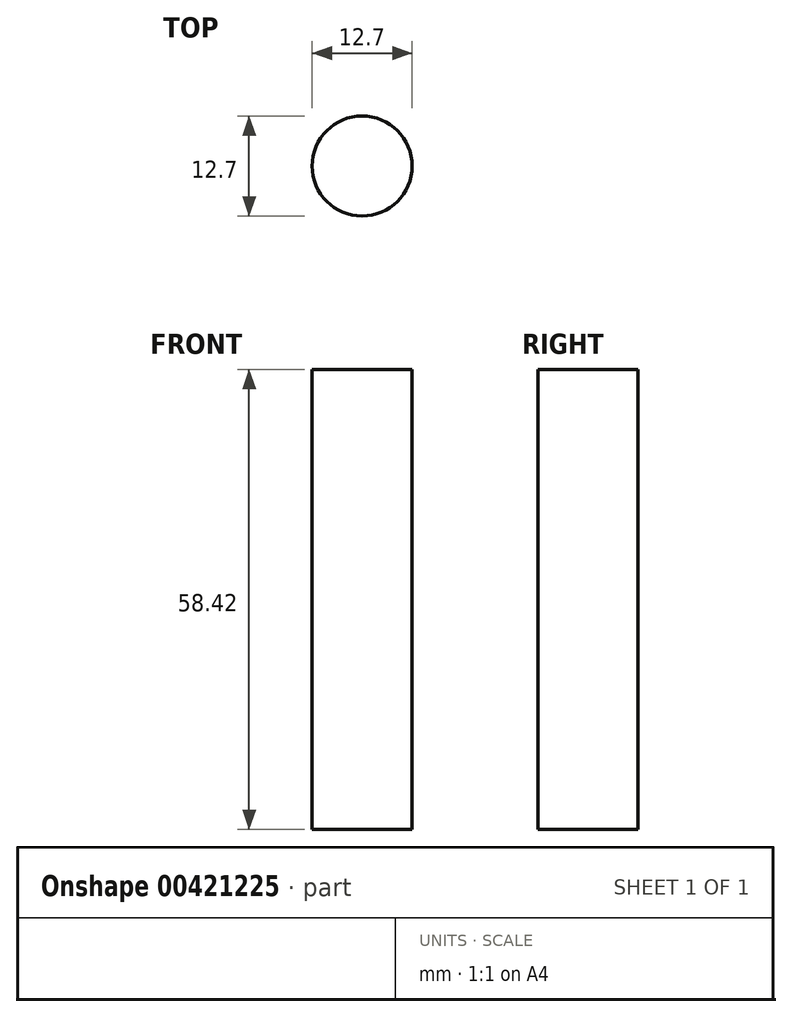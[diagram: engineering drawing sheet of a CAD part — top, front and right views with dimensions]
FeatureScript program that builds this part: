
annotation { "Feature Type Name" : "Feature", "Feature Type Description" : "" }
export const myFeature = defineFeature(function(context is Context, id is Id, definition is map)
    precondition{}
    {
        {
            var Q0;
            Q0=qCreatedBy(makeId("Top.planeOp"),FACE);
            var sketch = newSketch(context, id + "F0", { "sketchPlane" : qUnion([Q0])});
            skCircle(sketch, "E0", {"center": v(0, 0) * mm, "radius": 6.35 * mm});
            skSolve(sketch);
        }
        {
            var Q0;
            Q0 = qSketchRegion(id + "F0", true);
            extrude(context, id + "F1", {"entities" : qUnion([Q0]), "depth" : 58.42 * mm});
        }
    });
